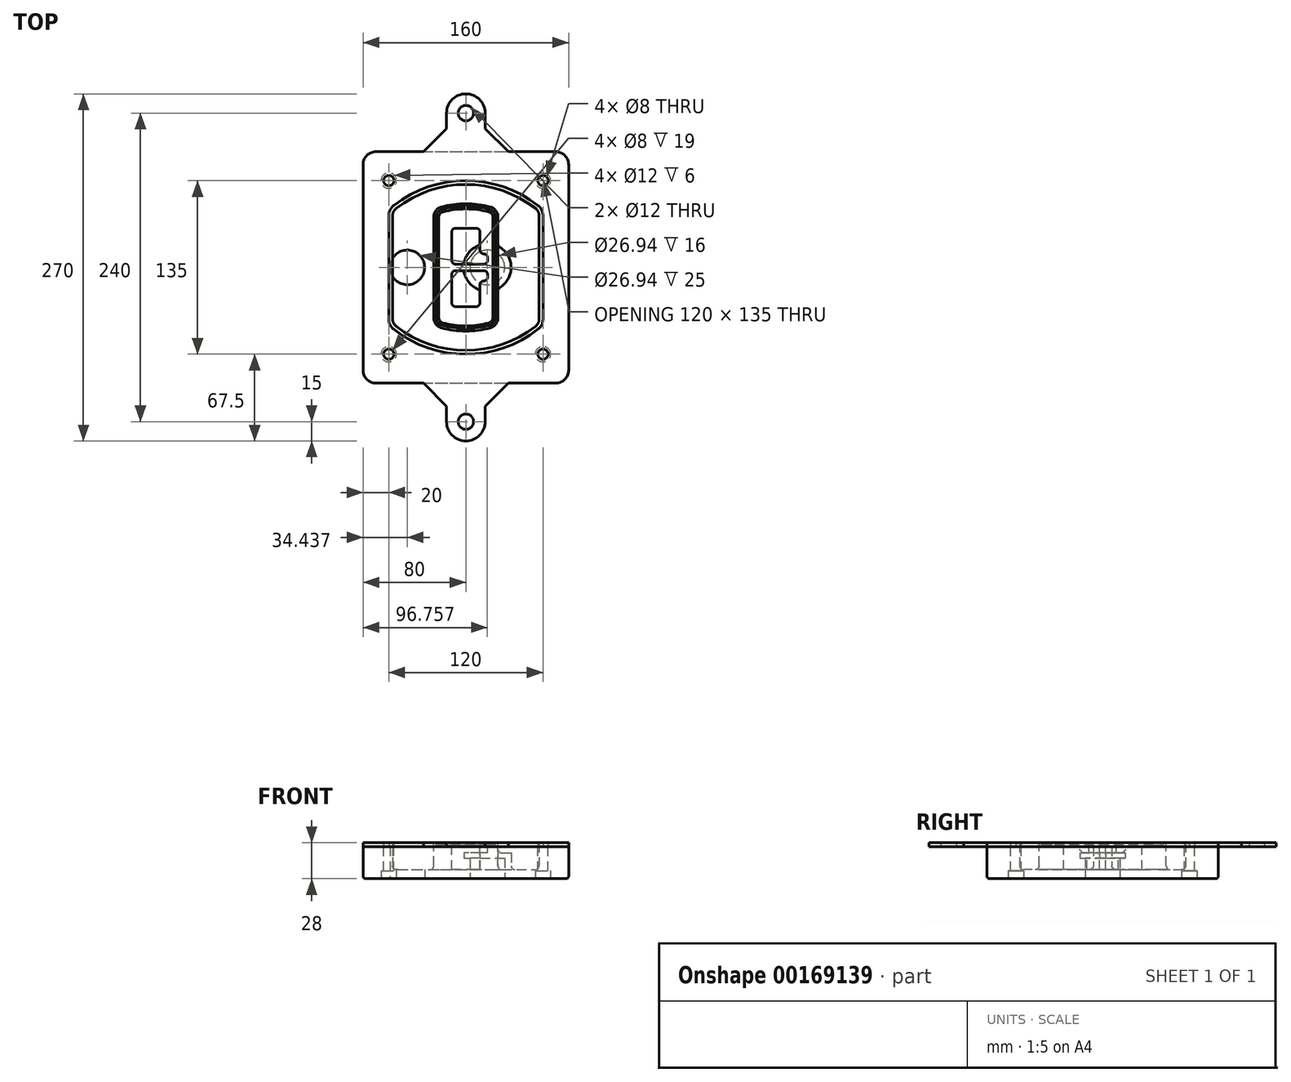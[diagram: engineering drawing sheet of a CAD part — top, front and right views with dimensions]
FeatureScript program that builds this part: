
annotation { "Feature Type Name" : "Feature", "Feature Type Description" : "" }
export const myFeature = defineFeature(function(context is Context, id is Id, definition is map)
    precondition{}
    {
        {
            var Q0;
            Q0=qCreatedBy(makeId("Top.planeOp"),FACE);
            var sketch = newSketch(context, id + "F0", { "sketchPlane" : qUnion([Q0])});
            skPoint(sketch, "E0.rect.middle", {"position": v(0, 0) * mm});
            skLineSegment(sketch, "E1.bottom", {"start": v(-70, -90) * mm, "end": v(70, -90) * mm});
            skLineSegment(sketch, "E1.top", {"start": v(-70, 90) * mm, "end": v(70, 90) * mm});
            skLineSegment(sketch, "E1.left", {"start": v(-80, -80) * mm, "end": v(-80, 80) * mm});
            skLineSegment(sketch, "E1.right", {"start": v(80, -80) * mm, "end": v(80, 80) * mm});
            skLineSegment(sketch, "E2", {"start": v(-80, 90) * mm, "end": v(80, -90) * mm, "construction": true});
            skLineSegment(sketch, "E3", {"start": v(80, 90) * mm, "end": v(-80, -90) * mm, "construction": true});
            skCircle(sketch, "E4", {"center": v(-60, 67.5) * mm, "radius": 4 * mm});
            skCircle(sketch, "E5", {"center": v(60, 67.5) * mm, "radius": 4 * mm});
            skCircle(sketch, "E6", {"center": v(60, -67.5) * mm, "radius": 4 * mm});
            skCircle(sketch, "E7", {"center": v(-60, -67.5) * mm, "radius": 4 * mm});
            skLineSegment(sketch, "E8", {"start": v(-60, 67.5) * mm, "end": v(60, 67.5) * mm, "construction": true});
            skLineSegment(sketch, "E9", {"start": v(60, 67.5) * mm, "end": v(60, -67.5) * mm, "construction": true});
            skLineSegment(sketch, "E10", {"start": v(60, -67.5) * mm, "end": v(-60, -67.5) * mm, "construction": true});
            skLineSegment(sketch, "E11", {"start": v(-60, -67.5) * mm, "end": v(-60, 67.5) * mm, "construction": true});
            skLineSegment(sketch, "E12", {"start": v(-60, 40.3) * mm, "end": v(-60, -40.3) * mm});
            skLineSegment(sketch, "E13", {"start": v(60, 40.3) * mm, "end": v(60, -40.3) * mm});
            skArc(sketch, "E14", {"start": v(56.15, 48.18) * mm, "mid": v(0, 67.5) * mm, "end": v(-56.15, 48.18) * mm});
            skArc(sketch, "E15", {"start": v(-56.15, -48.18) * mm, "mid": v(0, -67.5) * mm, "end": v(56.15, -48.18) * mm});
            skLineSegment(sketch, "E16", {"start": v(-60, 0) * mm, "end": v(60, 0) * mm, "construction": true});
            skPoint(sketch, "E17.visualSharp", {"position": v(-60, -45) * mm});
            skArc(sketch, "E17.filletArc", {"start": v(-60, -40.3) * mm, "mid": v(-58.99, -44.68) * mm, "end": v(-56.15, -48.18) * mm});
            skPoint(sketch, "E18.visualSharp", {"position": v(-60, 45) * mm});
            skArc(sketch, "E18.filletArc", {"start": v(-56.15, 48.18) * mm, "mid": v(-58.99, 44.68) * mm, "end": v(-60, 40.3) * mm});
            skPoint(sketch, "E19.visualSharp", {"position": v(60, 45) * mm});
            skArc(sketch, "E19.filletArc", {"start": v(60, 40.3) * mm, "mid": v(58.99, 44.68) * mm, "end": v(56.15, 48.18) * mm});
            skPoint(sketch, "E20.visualSharp", {"position": v(60, -45) * mm});
            skArc(sketch, "E20.filletArc", {"start": v(56.15, -48.18) * mm, "mid": v(58.99, -44.68) * mm, "end": v(60, -40.3) * mm});
            skPoint(sketch, "E21.visualSharp", {"position": v(-80, 90) * mm});
            skArc(sketch, "E21.filletArc", {"start": v(-70, 90) * mm, "mid": v(-77.07, 87.07) * mm, "end": v(-80, 80) * mm});
            skPoint(sketch, "E22.visualSharp", {"position": v(80, 90) * mm});
            skArc(sketch, "E22.filletArc", {"start": v(80, 80) * mm, "mid": v(77.07, 87.07) * mm, "end": v(70, 90) * mm});
            skPoint(sketch, "E23.visualSharp", {"position": v(80, -90) * mm});
            skArc(sketch, "E23.filletArc", {"start": v(70, -90) * mm, "mid": v(77.07, -87.07) * mm, "end": v(80, -80) * mm});
            skPoint(sketch, "E24.visualSharp", {"position": v(-80, -90) * mm});
            skArc(sketch, "E24.filletArc", {"start": v(-80, -80) * mm, "mid": v(-77.07, -87.07) * mm, "end": v(-70, -90) * mm});
            skArc(sketch, "E25.0", {"start": v(57, 40.3) * mm, "mid": v(56.3, 43.36) * mm, "end": v(54.3, 45.81) * mm});
            skLineSegment(sketch, "E25.1", {"start": v(57, 40.3) * mm, "end": v(57, -40.3) * mm});
            skArc(sketch, "E25.2", {"start": v(54.3, -45.81) * mm, "mid": v(56.3, -43.36) * mm, "end": v(57, -40.3) * mm});
            skArc(sketch, "E25.3", {"start": v(-54.3, -45.81) * mm, "mid": v(0, -64.5) * mm, "end": v(54.3, -45.81) * mm});
            skArc(sketch, "E25.4", {"start": v(-57, -40.3) * mm, "mid": v(-56.3, -43.36) * mm, "end": v(-54.3, -45.81) * mm});
            skArc(sketch, "E25.5", {"start": v(54.3, 45.81) * mm, "mid": v(0, 64.5) * mm, "end": v(-54.3, 45.81) * mm});
            skLineSegment(sketch, "E25.6", {"start": v(-57, 40.3) * mm, "end": v(-57, -40.3) * mm});
            skArc(sketch, "E25.7", {"start": v(-54.3, 45.81) * mm, "mid": v(-56.3, 43.36) * mm, "end": v(-57, 40.3) * mm});
            skArc(sketch, "E26.0", {"start": v(-58.62, 51.33) * mm, "mid": v(-62.58, 46.43) * mm, "end": v(-64, 40.3) * mm});
            skArc(sketch, "E26.1", {"start": v(58.62, 51.33) * mm, "mid": v(0, 71.5) * mm, "end": v(-58.62, 51.33) * mm});
            skArc(sketch, "E26.2", {"start": v(64, 40.3) * mm, "mid": v(62.58, 46.43) * mm, "end": v(58.62, 51.33) * mm});
            skLineSegment(sketch, "E26.3", {"start": v(64, 40.3) * mm, "end": v(64, -40.3) * mm});
            skArc(sketch, "E26.4", {"start": v(58.62, -51.33) * mm, "mid": v(62.58, -46.43) * mm, "end": v(64, -40.3) * mm});
            skLineSegment(sketch, "E26.5", {"start": v(-64, 40.3) * mm, "end": v(-64, -40.3) * mm});
            skArc(sketch, "E26.6", {"start": v(-58.62, -51.33) * mm, "mid": v(0, -71.5) * mm, "end": v(58.62, -51.33) * mm});
            skArc(sketch, "E26.7", {"start": v(-64, -40.3) * mm, "mid": v(-62.58, -46.43) * mm, "end": v(-58.62, -51.33) * mm});
            skSolve(sketch);
        }
        {
            var Q0;
            Q0=makeQuery(id+"F0.imprint","IMPRINT",FACE,{"disambiguationData":[TD([[makeQuery(id+"F0.imprint","IMPRINT",EDGE,{"derivedFrom":sQuery(id+"F0.wireOp",EDGE,"E1.bottom")}),1.0]])]});
            var Q1;
            Q1=makeQuery(id+"F0.imprint","IMPRINT",FACE,{"disambiguationData":[TD([[makeQuery(id+"F0.imprint","IMPRINT",EDGE,{"derivedFrom":sQuery(id+"F0.wireOp",EDGE,"E12")}),1.0]])]});
            var Q2;
            Q2=makeQuery(id+"F0.imprint","IMPRINT",FACE,{"disambiguationData":[TD([[makeQuery(id+"F0.imprint","IMPRINT",EDGE,{"derivedFrom":sQuery(id+"F0.wireOp",EDGE,"E25.0")}),1.0]])]});
            var Q3;
            Q3=makeQuery(id+"F0.imprint","IMPRINT",FACE,{"disambiguationData":[TD([[makeQuery(id+"F0.imprint","IMPRINT",EDGE,{"derivedFrom":sQuery(id+"F0.wireOp",EDGE,"E12")}),-1.0]])]});
            extrude(context, id + "F1", {"entities" : qUnion([Q0, Q1, Q2, Q3]), "oppositeDirection" : true, "depth" : 25 * mm});
        }
        {
            var Q0;
            Q0=makeQuery(id+"F0.imprint","IMPRINT",FACE,{"disambiguationData":[TD([[makeQuery(id+"F0.imprint","IMPRINT",EDGE,{"derivedFrom":sQuery(id+"F0.wireOp",EDGE,"E12")}),1.0]])]});
            extrude(context, id + "F2", {"entities" : qUnion([Q0]), "operationType" : NewBodyOperationType.ADD, "depth" : 3 * mm});
        }
        {
            var Q0;
            Q0=makeQuery(id+"F0.imprint","IMPRINT",FACE,{"disambiguationData":[TD([[makeQuery(id+"F0.imprint","IMPRINT",EDGE,{"derivedFrom":sQuery(id+"F0.wireOp",EDGE,"E25.0")}),1.0]])]});
            extrude(context, id + "F3", {"entities" : qUnion([Q0]), "operationType" : NewBodyOperationType.REMOVE, "oppositeDirection" : true, "depth" : 18 * mm});
        }
        {
            var Q0;
            Q0=makeQuery(id+"F2.opExtrude","CAP_FACE",FACE,{"disambiguationData":[OSD([sQuery(id+"F0.wireOp",EDGE,"E12"),sQuery(id+"F0.wireOp",EDGE,"E13"),sQuery(id+"F0.wireOp",EDGE,"E14"),sQuery(id+"F0.wireOp",EDGE,"E15"),sQuery(id+"F0.wireOp",EDGE,"E17.filletArc"),sQuery(id+"F0.wireOp",EDGE,"E18.filletArc"),sQuery(id+"F0.wireOp",EDGE,"E19.filletArc"),sQuery(id+"F0.wireOp",EDGE,"E20.filletArc"),sQuery(id+"F0.wireOp",EDGE,"E25.0"),sQuery(id+"F0.wireOp",EDGE,"E25.1"),sQuery(id+"F0.wireOp",EDGE,"E25.2"),sQuery(id+"F0.wireOp",EDGE,"E25.3"),sQuery(id+"F0.wireOp",EDGE,"E25.4"),sQuery(id+"F0.wireOp",EDGE,"E25.5"),sQuery(id+"F0.wireOp",EDGE,"E25.6"),sQuery(id+"F0.wireOp",EDGE,"E25.7")])],"isStart":false});
            var sketch = newSketch(context, id + "F4", { "sketchPlane" : qUnion([Q0])});
            skArc(sketch, "E27.0", {"start": v(-19.08, -46.97) * mm, "mid": v(0, -49.5) * mm, "end": v(19.08, -46.97) * mm});
            skArc(sketch, "E28.0", {"start": v(19.08, 46.97) * mm, "mid": v(0, 49.5) * mm, "end": v(-19.08, 46.97) * mm});
            skLineSegment(sketch, "E29", {"start": v(-25, 39.25) * mm, "end": v(-25, -39.25) * mm});
            skLineSegment(sketch, "E30", {"start": v(25, 39.25) * mm, "end": v(25, -39.25) * mm});
            skLineSegment(sketch, "E31", {"start": v(-25, 45.1) * mm, "end": v(25, 45.1) * mm, "construction": true});
            skLineSegment(sketch, "E32", {"start": v(-25, -45.1) * mm, "end": v(25, -45.1) * mm, "construction": true});
            skPoint(sketch, "E33.visualSharp", {"position": v(-25, 45.1) * mm});
            skArc(sketch, "E33.filletArc", {"start": v(-19.08, 46.97) * mm, "mid": v(-23.35, 44.11) * mm, "end": v(-25, 39.25) * mm});
            skPoint(sketch, "E34.visualSharp", {"position": v(25, 45.1) * mm});
            skArc(sketch, "E34.filletArc", {"start": v(25, 39.25) * mm, "mid": v(23.35, 44.11) * mm, "end": v(19.08, 46.97) * mm});
            skPoint(sketch, "E35.visualSharp", {"position": v(25, -45.1) * mm});
            skArc(sketch, "E35.filletArc", {"start": v(19.08, -46.97) * mm, "mid": v(23.35, -44.11) * mm, "end": v(25, -39.25) * mm});
            skPoint(sketch, "E36.visualSharp", {"position": v(-25, -45.1) * mm});
            skArc(sketch, "E36.filletArc", {"start": v(-25, -39.25) * mm, "mid": v(-23.35, -44.11) * mm, "end": v(-19.08, -46.97) * mm});
            skArc(sketch, "E37.0", {"start": v(54.3, 45.81) * mm, "mid": v(0, 64.5) * mm, "end": v(-54.3, 45.81) * mm});
            skArc(sketch, "E37.1", {"start": v(-54.3, 45.81) * mm, "mid": v(-56.3, 43.36) * mm, "end": v(-57, 40.3) * mm});
            skLineSegment(sketch, "E37.2", {"start": v(-57, 40.3) * mm, "end": v(-57, -40.3) * mm});
            skArc(sketch, "E37.3", {"start": v(-57, -40.3) * mm, "mid": v(-56.3, -43.36) * mm, "end": v(-54.3, -45.81) * mm});
            skArc(sketch, "E37.4", {"start": v(-54.3, -45.81) * mm, "mid": v(0, -64.5) * mm, "end": v(54.3, -45.81) * mm});
            skArc(sketch, "E37.5", {"start": v(54.3, -45.81) * mm, "mid": v(56.3, -43.36) * mm, "end": v(57, -40.3) * mm});
            skLineSegment(sketch, "E37.6", {"start": v(57, 40.3) * mm, "end": v(57, -40.3) * mm});
            skArc(sketch, "E37.7", {"start": v(57, 40.3) * mm, "mid": v(56.3, 43.36) * mm, "end": v(54.3, 45.81) * mm});
            skLineSegment(sketch, "E38.0", {"start": v(23, 39.25) * mm, "end": v(23, -39.25) * mm});
            skArc(sketch, "E38.1", {"start": v(18.56, -45.04) * mm, "mid": v(21.76, -42.9) * mm, "end": v(23, -39.25) * mm});
            skArc(sketch, "E38.2", {"start": v(-18.56, -45.04) * mm, "mid": v(0, -47.5) * mm, "end": v(18.56, -45.04) * mm});
            skArc(sketch, "E38.3", {"start": v(-23, -39.25) * mm, "mid": v(-21.76, -42.9) * mm, "end": v(-18.56, -45.04) * mm});
            skLineSegment(sketch, "E38.4", {"start": v(-23, 39.25) * mm, "end": v(-23, -39.25) * mm});
            skArc(sketch, "E38.5", {"start": v(23, 39.25) * mm, "mid": v(21.76, 42.9) * mm, "end": v(18.56, 45.04) * mm});
            skArc(sketch, "E38.6", {"start": v(-18.56, 45.04) * mm, "mid": v(-21.76, 42.9) * mm, "end": v(-23, 39.25) * mm});
            skArc(sketch, "E38.7", {"start": v(18.56, 45.04) * mm, "mid": v(0, 47.5) * mm, "end": v(-18.56, 45.04) * mm});
            skArc(sketch, "E39.0", {"start": v(21, 39.25) * mm, "mid": v(20.18, 41.68) * mm, "end": v(18.04, 43.1) * mm});
            skLineSegment(sketch, "E39.1", {"start": v(21, 39.25) * mm, "end": v(21, -39.25) * mm});
            skArc(sketch, "E39.2", {"start": v(18.04, -43.1) * mm, "mid": v(20.18, -41.68) * mm, "end": v(21, -39.25) * mm});
            skArc(sketch, "E39.3", {"start": v(-18.04, -43.1) * mm, "mid": v(0, -45.5) * mm, "end": v(18.04, -43.1) * mm});
            skArc(sketch, "E39.4", {"start": v(-21, -39.25) * mm, "mid": v(-20.18, -41.68) * mm, "end": v(-18.04, -43.1) * mm});
            skArc(sketch, "E39.5", {"start": v(18.04, 43.1) * mm, "mid": v(0, 45.5) * mm, "end": v(-18.04, 43.1) * mm});
            skLineSegment(sketch, "E39.6", {"start": v(-21, 39.25) * mm, "end": v(-21, -39.25) * mm});
            skArc(sketch, "E39.7", {"start": v(-18.04, 43.1) * mm, "mid": v(-20.18, 41.68) * mm, "end": v(-21, 39.25) * mm});
            skLineSegment(sketch, "E40", {"start": v(-25, 0) * mm, "end": v(25, 0) * mm, "construction": true});
            skLineSegment(sketch, "E41", {"start": v(-11, 5.5) * mm, "end": v(-11, 27.5) * mm});
            skLineSegment(sketch, "E42", {"start": v(-8, 30.5) * mm, "end": v(8, 30.5) * mm});
            skLineSegment(sketch, "E43", {"start": v(11, 27.5) * mm, "end": v(11, 13.5) * mm});
            skLineSegment(sketch, "E44", {"start": v(14, 10.5) * mm, "end": v(14, 10.5) * mm});
            skLineSegment(sketch, "E45", {"start": v(17, 7.5) * mm, "end": v(17, 5.5) * mm});
            skLineSegment(sketch, "E46", {"start": v(14, 2.5) * mm, "end": v(-8, 2.5) * mm});
            skPoint(sketch, "E47.visualSharp", {"position": v(-11, 30.5) * mm});
            skArc(sketch, "E47.filletArc", {"start": v(-8, 30.5) * mm, "mid": v(-10.12, 29.62) * mm, "end": v(-11, 27.5) * mm});
            skPoint(sketch, "E48.visualSharp", {"position": v(11, 30.5) * mm});
            skArc(sketch, "E48.filletArc", {"start": v(11, 27.5) * mm, "mid": v(10.12, 29.62) * mm, "end": v(8, 30.5) * mm});
            skPoint(sketch, "E49.visualSharp", {"position": v(11, 10.5) * mm});
            skArc(sketch, "E49.filletArc", {"start": v(11, 13.5) * mm, "mid": v(11.88, 11.38) * mm, "end": v(14, 10.5) * mm});
            skPoint(sketch, "E50.visualSharp", {"position": v(17, 10.5) * mm});
            skArc(sketch, "E50.filletArc", {"start": v(17, 7.5) * mm, "mid": v(16.12, 9.62) * mm, "end": v(14, 10.5) * mm});
            skPoint(sketch, "E51.visualSharp", {"position": v(17, 2.5) * mm});
            skArc(sketch, "E51.filletArc", {"start": v(14, 2.5) * mm, "mid": v(16.12, 3.38) * mm, "end": v(17, 5.5) * mm});
            skPoint(sketch, "E52.visualSharp", {"position": v(-11, 2.5) * mm});
            skArc(sketch, "E52.filletArc", {"start": v(-11, 5.5) * mm, "mid": v(-10.12, 3.38) * mm, "end": v(-8, 2.5) * mm});
            skLineSegment(sketch, "E53.0.MirrorCS", {"start": v(14, -2.5) * mm, "end": v(-8, -2.5) * mm});
            skArc(sketch, "E54.0.MirrorCS", {"start": v(-11, -5.5) * mm, "mid": v(-10.12, -3.38) * mm, "end": v(-8, -2.5) * mm});
            skLineSegment(sketch, "E55.0.MirrorCS", {"start": v(-11, -5.5) * mm, "end": v(-11, -27.5) * mm});
            skArc(sketch, "E56.0.MirrorCS", {"start": v(-8, -30.5) * mm, "mid": v(-10.12, -29.62) * mm, "end": v(-11, -27.5) * mm});
            skLineSegment(sketch, "E57.0.MirrorCS", {"start": v(-8, -30.5) * mm, "end": v(8, -30.5) * mm});
            skArc(sketch, "E58.0.MirrorCS", {"start": v(11, -27.5) * mm, "mid": v(10.12, -29.62) * mm, "end": v(8, -30.5) * mm});
            skLineSegment(sketch, "E59.0.MirrorCS", {"start": v(11, -27.5) * mm, "end": v(11, -13.5) * mm});
            skArc(sketch, "E60.0.MirrorCS", {"start": v(11, -13.5) * mm, "mid": v(11.88, -11.38) * mm, "end": v(14, -10.5) * mm});
            skArc(sketch, "E61.0.MirrorCS", {"start": v(17, -7.5) * mm, "mid": v(16.12, -9.62) * mm, "end": v(14, -10.5) * mm});
            skLineSegment(sketch, "E62.0.MirrorCS", {"start": v(17, -7.5) * mm, "end": v(17, -5.5) * mm});
            skArc(sketch, "E63.0.MirrorCS", {"start": v(14, -2.5) * mm, "mid": v(16.12, -3.38) * mm, "end": v(17, -5.5) * mm});
            skSolve(sketch);
        }
        {
            var Q0;
            Q0=makeQuery(id+"F4.imprint","IMPRINT",FACE,{"disambiguationData":[TD([[makeQuery(id+"F4.imprint","IMPRINT",EDGE,{"derivedFrom":sQuery(id+"F4.wireOp",EDGE,"E27.0")}),1.0]])]});
            var Q1;
            Q1=makeQuery(id+"F4.imprint","IMPRINT",FACE,{"disambiguationData":[TD([[makeQuery(id+"F4.imprint","IMPRINT",EDGE,{"derivedFrom":sQuery(id+"F4.wireOp",EDGE,"E38.0")}),-1.0]])]});
            var Q2;
            Q2=makeQuery(id+"F4.imprint","IMPRINT",FACE,{"disambiguationData":[TD([[makeQuery(id+"F4.imprint","IMPRINT",EDGE,{"derivedFrom":sQuery(id+"F4.wireOp",EDGE,"E39.0")}),1.0]])]});
            extrude(context, id + "F5", {"entities" : qUnion([Q0, Q1, Q2]), "operationType" : NewBodyOperationType.ADD, "endBound" : BoundingType.UP_TO_NEXT, "oppositeDirection" : true, "depth" : 25 * mm});
        }
        {
            var Q0;
            Q0=makeQuery(id+"F4.imprint","IMPRINT",FACE,{"disambiguationData":[TD([[makeQuery(id+"F4.imprint","IMPRINT",EDGE,{"derivedFrom":sQuery(id+"F4.wireOp",EDGE,"E38.0")}),-1.0]])]});
            extrude(context, id + "F6", {"entities" : qUnion([Q0]), "operationType" : NewBodyOperationType.REMOVE, "oppositeDirection" : true, "depth" : 2 * mm});
        }
        {
            var Q0;
            Q0=makeQuery(id+"F1.opExtrude","CAP_FACE",FACE,{"disambiguationData":[OSD([sQuery(id+"F0.wireOp",EDGE,"E1.bottom"),sQuery(id+"F0.wireOp",EDGE,"E1.top"),sQuery(id+"F0.wireOp",EDGE,"E1.left"),sQuery(id+"F0.wireOp",EDGE,"E1.right"),sQuery(id+"F0.wireOp",EDGE,"E4"),sQuery(id+"F0.wireOp",EDGE,"E5"),sQuery(id+"F0.wireOp",EDGE,"E6"),sQuery(id+"F0.wireOp",EDGE,"E7"),sQuery(id+"F0.wireOp",EDGE,"E21.filletArc"),sQuery(id+"F0.wireOp",EDGE,"E22.filletArc"),sQuery(id+"F0.wireOp",EDGE,"E23.filletArc"),sQuery(id+"F0.wireOp",EDGE,"E24.filletArc")])],"isStart":false});
            var sketch = newSketch(context, id + "F7", { "sketchPlane" : qUnion([Q0])});
            skCircle(sketch, "E64", {"center": v(16.76, 0) * mm, "radius": 13.47 * mm});
            skCircle(sketch, "E65", {"center": v(-45.56, 0) * mm, "radius": 13.47 * mm});
            skLineSegment(sketch, "E66", {"start": v(80, 0) * mm, "end": v(-80, 0) * mm});
            skCircle(sketch, "E67", {"center": v(16.76, 0) * mm, "radius": 18.47 * mm});
            skCircle(sketch, "E68", {"center": v(60, -67.5) * mm, "radius": 6 * mm});
            skCircle(sketch, "E69", {"center": v(-60, -67.5) * mm, "radius": 6 * mm});
            skCircle(sketch, "E70", {"center": v(-60, 67.5) * mm, "radius": 6 * mm});
            skCircle(sketch, "E71", {"center": v(60, 67.5) * mm, "radius": 6 * mm});
            skSolve(sketch);
        }
        {
            var Q0;
            {var subQ1=sQuery(id+"F7.wireOp",EDGE,"E66");var subQ4=sQuery(id+"F7.wireOp",EDGE,"E64");var subQ6=makeQuery(id+"F7.imprint","INTERSECT",VERTEX,{"disambiguationData":[OD(0.0)],"derivedFrom":[subQ4,subQ1]});Q0=makeQuery(id+"F7.imprint","IMPRINT",FACE,{"disambiguationData":[TD([[makeQuery(id+"F7.imprint","IMPRINT",EDGE,{"disambiguationData":[TD([[subQ6,-1.0]])],"derivedFrom":subQ4}),-1.0]])]});}
            var Q1;
            {var subQ0=sQuery(id+"F7.wireOp",EDGE,"E66");var subQ1=sQuery(id+"F7.wireOp",EDGE,"E64");var subQ3=makeQuery(id+"F7.imprint","INTERSECT",VERTEX,{"disambiguationData":[OD(0.0)],"derivedFrom":[subQ1,subQ0]});Q1=makeQuery(id+"F7.imprint","IMPRINT",FACE,{"disambiguationData":[TD([[makeQuery(id+"F7.imprint","IMPRINT",EDGE,{"disambiguationData":[TD([[subQ3,-1.0]])],"derivedFrom":subQ1}),1.0]])]});}
            var Q2;
            {var subQ0=sQuery(id+"F7.wireOp",EDGE,"E66");var subQ1=sQuery(id+"F7.wireOp",EDGE,"E64");var subQ3=makeQuery(id+"F7.imprint","INTERSECT",VERTEX,{"disambiguationData":[OD(0.0)],"derivedFrom":[subQ1,subQ0]});Q2=makeQuery(id+"F7.imprint","IMPRINT",FACE,{"disambiguationData":[TD([[makeQuery(id+"F7.imprint","IMPRINT",EDGE,{"disambiguationData":[TD([[subQ3,1.0]])],"derivedFrom":subQ1}),1.0]])]});}
            var Q3;
            {var subQ1=sQuery(id+"F7.wireOp",EDGE,"E66");var subQ4=sQuery(id+"F7.wireOp",EDGE,"E64");var subQ6=makeQuery(id+"F7.imprint","INTERSECT",VERTEX,{"disambiguationData":[OD(0.0)],"derivedFrom":[subQ4,subQ1]});Q3=makeQuery(id+"F7.imprint","IMPRINT",FACE,{"disambiguationData":[TD([[makeQuery(id+"F7.imprint","IMPRINT",EDGE,{"disambiguationData":[TD([[subQ6,1.0]])],"derivedFrom":subQ4}),-1.0]])]});}
            extrude(context, id + "F8", {"entities" : qUnion([Q0, Q1, Q2, Q3]), "operationType" : NewBodyOperationType.ADD, "oppositeDirection" : true, "depth" : 20 * mm});
        }
        {
            var Q0;
            {var subQ0=sQuery(id+"F7.wireOp",EDGE,"E66");var subQ1=sQuery(id+"F7.wireOp",EDGE,"E64");var subQ3=makeQuery(id+"F7.imprint","INTERSECT",VERTEX,{"disambiguationData":[OD(0.0)],"derivedFrom":[subQ1,subQ0]});Q0=makeQuery(id+"F7.imprint","IMPRINT",FACE,{"disambiguationData":[TD([[makeQuery(id+"F7.imprint","IMPRINT",EDGE,{"disambiguationData":[TD([[subQ3,-1.0]])],"derivedFrom":subQ1}),1.0]])]});}
            var Q1;
            {var subQ0=sQuery(id+"F7.wireOp",EDGE,"E66");var subQ1=sQuery(id+"F7.wireOp",EDGE,"E64");var subQ3=makeQuery(id+"F7.imprint","INTERSECT",VERTEX,{"disambiguationData":[OD(0.0)],"derivedFrom":[subQ1,subQ0]});Q1=makeQuery(id+"F7.imprint","IMPRINT",FACE,{"disambiguationData":[TD([[makeQuery(id+"F7.imprint","IMPRINT",EDGE,{"disambiguationData":[TD([[subQ3,1.0]])],"derivedFrom":subQ1}),1.0]])]});}
            extrude(context, id + "F9", {"entities" : qUnion([Q0, Q1]), "operationType" : NewBodyOperationType.REMOVE, "oppositeDirection" : true, "depth" : 16 * mm});
        }
        {
            var Q0;
            {var subQ0=sQuery(id+"F7.wireOp",EDGE,"E66");var subQ1=sQuery(id+"F7.wireOp",EDGE,"E65");var subQ3=makeQuery(id+"F7.imprint","INTERSECT",VERTEX,{"disambiguationData":[OD(0.0)],"derivedFrom":[subQ1,subQ0]});Q0=makeQuery(id+"F7.imprint","IMPRINT",FACE,{"disambiguationData":[TD([[makeQuery(id+"F7.imprint","IMPRINT",EDGE,{"disambiguationData":[TD([[subQ3,-1.0]])],"derivedFrom":subQ1}),1.0]])]});}
            var Q1;
            {var subQ0=sQuery(id+"F7.wireOp",EDGE,"E66");var subQ1=sQuery(id+"F7.wireOp",EDGE,"E65");var subQ3=makeQuery(id+"F7.imprint","INTERSECT",VERTEX,{"disambiguationData":[OD(0.0)],"derivedFrom":[subQ1,subQ0]});Q1=makeQuery(id+"F7.imprint","IMPRINT",FACE,{"disambiguationData":[TD([[makeQuery(id+"F7.imprint","IMPRINT",EDGE,{"disambiguationData":[TD([[subQ3,1.0]])],"derivedFrom":subQ1}),1.0]])]});}
            extrude(context, id + "F10", {"entities" : qUnion([Q0, Q1]), "operationType" : NewBodyOperationType.REMOVE, "oppositeDirection" : true, "depth" : 25 * mm});
        }
        {
            var Q0;
            Q0=makeQuery(id+"F7.imprint","IMPRINT",FACE,{"disambiguationData":[TD([[makeQuery(id+"F7.imprint","IMPRINT",EDGE,{"derivedFrom":sQuery(id+"F7.wireOp",EDGE,"E68")}),1.0]])]});
            var Q1;
            Q1=makeQuery(id+"F7.imprint","IMPRINT",FACE,{"disambiguationData":[TD([[makeQuery(id+"F7.imprint","IMPRINT",EDGE,{"derivedFrom":makeQuery(id+"F1.opExtrude","CAP_EDGE",EDGE,{"disambiguationData":[OSD([sQuery(id+"F0.wireOp",EDGE,"E5")])],"isStart":false})}),-1.0]])]});
            var Q2;
            Q2=makeQuery(id+"F7.imprint","IMPRINT",FACE,{"disambiguationData":[TD([[makeQuery(id+"F7.imprint","IMPRINT",EDGE,{"derivedFrom":sQuery(id+"F7.wireOp",EDGE,"E69")}),1.0]])]});
            var Q3;
            Q3=makeQuery(id+"F7.imprint","IMPRINT",FACE,{"disambiguationData":[TD([[makeQuery(id+"F7.imprint","IMPRINT",EDGE,{"derivedFrom":makeQuery(id+"F1.opExtrude","CAP_EDGE",EDGE,{"disambiguationData":[OSD([sQuery(id+"F0.wireOp",EDGE,"E4")])],"isStart":false})}),-1.0]])]});
            var Q4;
            Q4=makeQuery(id+"F7.imprint","IMPRINT",FACE,{"disambiguationData":[TD([[makeQuery(id+"F7.imprint","IMPRINT",EDGE,{"derivedFrom":sQuery(id+"F7.wireOp",EDGE,"E70")}),1.0]])]});
            var Q5;
            Q5=makeQuery(id+"F7.imprint","IMPRINT",FACE,{"disambiguationData":[TD([[makeQuery(id+"F7.imprint","IMPRINT",EDGE,{"derivedFrom":makeQuery(id+"F1.opExtrude","CAP_EDGE",EDGE,{"disambiguationData":[OSD([sQuery(id+"F0.wireOp",EDGE,"E7")])],"isStart":false})}),-1.0]])]});
            var Q6;
            Q6=makeQuery(id+"F7.imprint","IMPRINT",FACE,{"disambiguationData":[TD([[makeQuery(id+"F7.imprint","IMPRINT",EDGE,{"derivedFrom":sQuery(id+"F7.wireOp",EDGE,"E71")}),1.0]])]});
            var Q7;
            Q7=makeQuery(id+"F7.imprint","IMPRINT",FACE,{"disambiguationData":[TD([[makeQuery(id+"F7.imprint","IMPRINT",EDGE,{"derivedFrom":makeQuery(id+"F1.opExtrude","CAP_EDGE",EDGE,{"disambiguationData":[OSD([sQuery(id+"F0.wireOp",EDGE,"E6")])],"isStart":false})}),-1.0]])]});
            extrude(context, id + "F11", {"entities" : qUnion([Q0, Q1, Q2, Q3, Q4, Q5, Q6, Q7]), "operationType" : NewBodyOperationType.REMOVE, "oppositeDirection" : true, "depth" : 6 * mm});
        }
        {
            var Q0;
            Q0=makeQuery(id+"F9.boolean.opBoolean","COPY",FACE,{"derivedFrom":makeQuery(id+"F9.opExtrude","CAP_FACE",FACE,{"disambiguationData":[OSD([sQuery(id+"F7.wireOp",EDGE,"E64")])],"isStart":false})});
            var sketch = newSketch(context, id + "F12", { "sketchPlane" : qUnion([Q0])});
            skArc(sketch, "E72.0", {"start": v(11, 17.55) * mm, "mid": v(2.57, 11.82) * mm, "end": v(-1.54, 2.5) * mm});
            skArc(sketch, "E72.1", {"start": v(-1.54, -2.5) * mm, "mid": v(2.57, -11.82) * mm, "end": v(11, -17.55) * mm});
            skLineSegment(sketch, "E73", {"start": v(-1.54, -2.5) * mm, "end": v(14, -2.5) * mm});
            skLineSegment(sketch, "E74.0", {"start": v(14, 2.5) * mm, "end": v(-1.54, 2.5) * mm});
            skArc(sketch, "E74.1", {"start": v(14, 2.5) * mm, "mid": v(16.12, 3.38) * mm, "end": v(17, 5.5) * mm});
            skLineSegment(sketch, "E74.2", {"start": v(17, 7.5) * mm, "end": v(17, 5.5) * mm});
            skArc(sketch, "E74.3", {"start": v(17, 7.5) * mm, "mid": v(16.12, 9.62) * mm, "end": v(14, 10.5) * mm});
            skArc(sketch, "E74.4", {"start": v(11, 13.5) * mm, "mid": v(11.88, 11.38) * mm, "end": v(14, 10.5) * mm});
            skLineSegment(sketch, "E74.5", {"start": v(11, 17.55) * mm, "end": v(11, 13.5) * mm});
            skLineSegment(sketch, "E74.7", {"start": v(14, -2.5) * mm, "end": v(-1.54, -2.5) * mm});
            skArc(sketch, "E74.8", {"start": v(14, -2.5) * mm, "mid": v(16.12, -3.38) * mm, "end": v(17, -5.5) * mm});
            skLineSegment(sketch, "E74.9", {"start": v(17, -7.5) * mm, "end": v(17, -5.5) * mm});
            skArc(sketch, "E74.10", {"start": v(17, -7.5) * mm, "mid": v(16.12, -9.62) * mm, "end": v(14, -10.5) * mm});
            skArc(sketch, "E74.11", {"start": v(11, -13.5) * mm, "mid": v(11.88, -11.38) * mm, "end": v(14, -10.5) * mm});
            skLineSegment(sketch, "E74.12", {"start": v(11, -17.55) * mm, "end": v(11, -13.5) * mm});
            skPoint(sketch, "E75.orphan", {"position": v(11, -27.5) * mm});
            skPoint(sketch, "E76.orphan", {"position": v(-8, -2.5) * mm});
            skPoint(sketch, "E77.orphan", {"position": v(-8, 2.5) * mm});
            skPoint(sketch, "E78.orphan", {"position": v(11, 27.5) * mm});
            skSolve(sketch);
        }
        {
            var Q0;
            {var subQ7=sQuery(id+"F12.wireOp",EDGE,"E72.0");var subQ14=sQuery(id+"F12.wireOp",EDGE,"E72.1");var subQ16=sQuery(id+"F12.wireOp",EDGE,"E74.1");var subQ18=sQuery(id+"F12.wireOp",EDGE,"E74.8");Q0=qUnion([makeQuery(id+"F12.imprint","IMPRINT",FACE,{"disambiguationData":[TD([[makeQuery(id+"F12.imprint","IMPRINT",EDGE,{"derivedFrom":subQ7}),1.0]])]}),makeQuery(id+"F12.imprint","IMPRINT",FACE,{"disambiguationData":[TD([[makeQuery(id+"F12.imprint","IMPRINT",EDGE,{"derivedFrom":subQ14}),1.0]])]}),makeQuery(id+"F12.imprint","IMPRINT",FACE,{"disambiguationData":[TD([[makeQuery(id+"F12.imprint","IMPRINT",EDGE,{"derivedFrom":subQ16}),1.0]])]}),makeQuery(id+"F12.imprint","IMPRINT",FACE,{"disambiguationData":[TD([[makeQuery(id+"F12.imprint","IMPRINT",EDGE,{"derivedFrom":subQ18}),-1.0]])]})]);}
            var Q1;
            Q1=makeQuery(id+"F5.boolean.opBoolean","SPLIT",FACE,{"disambiguationData":[TD([makeQuery(id+"F5.opExtrude","SWEPT_FACE",FACE,{"disambiguationData":[OSD([sQuery(id+"F4.wireOp",EDGE,"E41")])]})])],"derivedFrom":makeQuery(id+"F3.boolean.opBoolean","COPY",FACE,{"derivedFrom":makeQuery(id+"F3.opExtrude","CAP_FACE",FACE,{"disambiguationData":[OSD([sQuery(id+"F0.wireOp",EDGE,"E25.0"),sQuery(id+"F0.wireOp",EDGE,"E25.1"),sQuery(id+"F0.wireOp",EDGE,"E25.2"),sQuery(id+"F0.wireOp",EDGE,"E25.3"),sQuery(id+"F0.wireOp",EDGE,"E25.4"),sQuery(id+"F0.wireOp",EDGE,"E25.5"),sQuery(id+"F0.wireOp",EDGE,"E25.6"),sQuery(id+"F0.wireOp",EDGE,"E25.7")])],"isStart":false})})});
            extrude(context, id + "F13", {"entities" : qUnion([Q0]), "operationType" : NewBodyOperationType.REMOVE, "endBound" : BoundingType.UP_TO_SURFACE, "endBoundEntityFace" : qUnion([Q1]), "depth" : 25 * mm});
        }
        {
            var Q0;
            Q0=makeQuery(id+"F3.boolean.opBoolean","COPY",EDGE,{"derivedFrom":makeQuery(id+"F3.opExtrude","CAP_EDGE",EDGE,{"disambiguationData":[OSD([sQuery(id+"F0.wireOp",EDGE,"E25.6")])],"isStart":false})});
            var Q1;
            Q1=makeQuery(id+"F8.boolean.opBoolean","INTERSECT",EDGE,{"derivedFrom":[makeQuery(id+"F5.opExtrude","SWEPT_FACE",FACE,{"disambiguationData":[OSD([sQuery(id+"F4.wireOp",EDGE,"E30")])]}),makeQuery(id+"F8.opExtrude","CAP_FACE",FACE,{"disambiguationData":[OSD([sQuery(id+"F7.wireOp",EDGE,"E67")])],"isStart":false})]});
            var Q2;
            Q2=makeQuery(id+"F8.boolean.opBoolean","INTERSECT",EDGE,{"disambiguationData":[OD(1.0)],"derivedFrom":[makeQuery(id+"F5.opExtrude","SWEPT_FACE",FACE,{"disambiguationData":[OSD([sQuery(id+"F4.wireOp",EDGE,"E30")])]}),makeQuery(id+"F8.opExtrude","SWEPT_FACE",FACE,{"disambiguationData":[OSD([sQuery(id+"F7.wireOp",EDGE,"E67")])]})]});
            var Q3;
            {var subQ0=sQuery(id+"F4.wireOp",EDGE,"E30");Q3=makeQuery(id+"F8.boolean.opBoolean","SPLIT",EDGE,{"disambiguationData":[TD([makeQuery(id+"F5.opExtrude","SWEPT_FACE",FACE,{"disambiguationData":[OSD([sQuery(id+"F4.wireOp",EDGE,"E35.filletArc")])]})])],"derivedFrom":makeQuery(id+"F5.opExtrude","CAP_EDGE",EDGE,{"disambiguationData":[OSD([subQ0])],"isStart":false})});}
            var Q4;
            {var subQ0=sQuery(id+"F0.wireOp",EDGE,"E25.7");var subQ1=sQuery(id+"F0.wireOp",EDGE,"E25.1");var subQ2=sQuery(id+"F0.wireOp",EDGE,"E25.6");var subQ3=sQuery(id+"F0.wireOp",EDGE,"E25.5");var subQ4=sQuery(id+"F0.wireOp",EDGE,"E25.4");var subQ5=sQuery(id+"F0.wireOp",EDGE,"E25.0");var subQ6=sQuery(id+"F0.wireOp",EDGE,"E25.2");var subQ7=sQuery(id+"F0.wireOp",EDGE,"E25.3");Q4=makeQuery(id+"F8.boolean.opBoolean","INTERSECT",EDGE,{"derivedFrom":[makeQuery(id+"F5.boolean.opBoolean","SPLIT",FACE,{"disambiguationData":[TD([makeQuery(id+"F2.opExtrude","SWEPT_FACE",FACE,{"disambiguationData":[OSD([subQ5])]})])],"derivedFrom":makeQuery(id+"F3.boolean.opBoolean","COPY",FACE,{"derivedFrom":makeQuery(id+"F3.opExtrude","CAP_FACE",FACE,{"disambiguationData":[OSD([subQ5,subQ1,subQ6,subQ7,subQ4,subQ3,subQ2,subQ0])],"isStart":false})})}),makeQuery(id+"F8.opExtrude","SWEPT_FACE",FACE,{"disambiguationData":[OSD([sQuery(id+"F7.wireOp",EDGE,"E67")])]})]});}
            var Q5;
            Q5=makeQuery(id+"F8.boolean.opBoolean","INTERSECT",EDGE,{"disambiguationData":[OD(0.0)],"derivedFrom":[makeQuery(id+"F5.opExtrude","SWEPT_FACE",FACE,{"disambiguationData":[OSD([sQuery(id+"F4.wireOp",EDGE,"E30")])]}),makeQuery(id+"F8.opExtrude","SWEPT_FACE",FACE,{"disambiguationData":[OSD([sQuery(id+"F7.wireOp",EDGE,"E67")])]})]});
            fillet(context, id + "F14", {"entities" : qUnion([Q0, Q1, Q2, Q3, Q4, Q5]), "radius" : 3 * mm, "tangentPropagation" : true, "allowEdgeOverflow" : false});
        }
        {
            var Q0;
            Q0=makeQuery(id+"F1.opExtrude","CAP_EDGE",EDGE,{"disambiguationData":[OSD([sQuery(id+"F0.wireOp",EDGE,"E1.bottom")])],"isStart":false});
            fillet(context, id + "F15", {"entities" : qUnion([Q0]), "radius" : 2 * mm, "tangentPropagation" : true, "allowEdgeOverflow" : false});
        }
        {
            var Q0;
            {var subQ0=sQuery(id+"F0.wireOp",EDGE,"E22.filletArc");var subQ1=sQuery(id+"F0.wireOp",EDGE,"E7");var subQ2=sQuery(id+"F0.wireOp",EDGE,"E6");var subQ3=sQuery(id+"F0.wireOp",EDGE,"E5");var subQ4=sQuery(id+"F0.wireOp",EDGE,"E4");var subQ5=sQuery(id+"F0.wireOp",EDGE,"E1.bottom");var subQ6=sQuery(id+"F0.wireOp",EDGE,"E21.filletArc");var subQ7=sQuery(id+"F0.wireOp",EDGE,"E1.top");var subQ8=sQuery(id+"F0.wireOp",EDGE,"E1.left");var subQ9=sQuery(id+"F0.wireOp",EDGE,"E1.right");var subQ10=sQuery(id+"F0.wireOp",EDGE,"E23.filletArc");var subQ11=sQuery(id+"F0.wireOp",EDGE,"E24.filletArc");Q0=makeQuery(id+"F2.boolean.opBoolean","SPLIT",FACE,{"disambiguationData":[TD([makeQuery(id+"F1.opExtrude","SWEPT_FACE",FACE,{"disambiguationData":[OSD([subQ5])]})])],"derivedFrom":makeQuery(id+"F1.opExtrude","CAP_FACE",FACE,{"disambiguationData":[OSD([subQ5,subQ7,subQ8,subQ9,subQ4,subQ3,subQ2,subQ1,subQ6,subQ0,subQ10,subQ11])],"isStart":true})});}
            var sketch = newSketch(context, id + "F16", { "sketchPlane" : qUnion([Q0])});
            skCircle(sketch, "E79", {"center": v(0, 120) * mm, "radius": 6 * mm});
            skArc(sketch, "E80", {"start": v(15, 120) * mm, "mid": v(0, 135) * mm, "end": v(-15, 120) * mm});
            skLineSegment(sketch, "E81", {"start": v(-15, 120) * mm, "end": v(-15, 108) * mm});
            skLineSegment(sketch, "E82", {"start": v(-15, 108) * mm, "end": v(-33, 90) * mm});
            skLineSegment(sketch, "E83", {"start": v(0, 120) * mm, "end": v(0, 90) * mm, "construction": true});
            skLineSegment(sketch, "E84", {"start": v(15, 108) * mm, "end": v(33, 90) * mm});
            skLineSegment(sketch, "E85", {"start": v(-80, 0) * mm, "end": v(80, 0) * mm, "construction": true});
            skArc(sketch, "E86.MirrorCS", {"start": v(15, -120) * mm, "mid": v(0, -135) * mm, "end": v(-15, -120) * mm});
            skLineSegment(sketch, "E87.MirrorCS", {"start": v(-15, -120) * mm, "end": v(-15, -108) * mm});
            skCircle(sketch, "E88.MirrorC", {"center": v(0, -120) * mm, "radius": 6 * mm});
            skLineSegment(sketch, "E89.MirrorCS", {"start": v(15, -120) * mm, "end": v(15, -108) * mm, "construction": true});
            skLineSegment(sketch, "E90", {"start": v(15, 120) * mm, "end": v(15, 108) * mm});
            skLineSegment(sketch, "E91.MirrorCS", {"start": v(15, -120) * mm, "end": v(15, -108) * mm});
            skLineSegment(sketch, "E92.MirrorCS", {"start": v(-15, -108) * mm, "end": v(-33, -90) * mm});
            skLineSegment(sketch, "E93.MirrorCS", {"start": v(15, -108) * mm, "end": v(33, -90) * mm});
            skLineSegment(sketch, "E94.MirrorCS", {"start": v(15, 120) * mm, "end": v(15, 108) * mm, "construction": true});
            skLineSegment(sketch, "E95.MirrorCS", {"start": v(15, 92.25) * mm, "end": v(33, 74.25) * mm});
            skSolve(sketch);
        }
        {
            var Q0;
            Q0=makeQuery(id+"F16.imprint","IMPRINT",FACE,{"disambiguationData":[TD([[makeQuery(id+"F16.imprint","IMPRINT",EDGE,{"derivedFrom":sQuery(id+"F16.wireOp",EDGE,"E91.MirrorCS")}),1.0]])]});
            var Q1;
            Q1=makeQuery(id+"F16.imprint","IMPRINT",FACE,{"disambiguationData":[TD([[makeQuery(id+"F16.imprint","IMPRINT",EDGE,{"derivedFrom":makeQuery(id+"F1.opExtrude","CAP_EDGE",EDGE,{"disambiguationData":[OSD([sQuery(id+"F0.wireOp",EDGE,"E1.left")])],"isStart":true})}),-1.0]])]});
            var Q2;
            Q2=makeQuery(id+"F16.imprint","IMPRINT",FACE,{"disambiguationData":[TD([[makeQuery(id+"F16.imprint","IMPRINT",EDGE,{"derivedFrom":sQuery(id+"F16.wireOp",EDGE,"E79")}),-1.0]])]});
            var Q3;
            Q3=makeQuery(id+"F2.opExtrude","CAP_FACE",FACE,{"disambiguationData":[OSD([sQuery(id+"F0.wireOp",EDGE,"E12"),sQuery(id+"F0.wireOp",EDGE,"E13"),sQuery(id+"F0.wireOp",EDGE,"E14"),sQuery(id+"F0.wireOp",EDGE,"E15"),sQuery(id+"F0.wireOp",EDGE,"E17.filletArc"),sQuery(id+"F0.wireOp",EDGE,"E18.filletArc"),sQuery(id+"F0.wireOp",EDGE,"E19.filletArc"),sQuery(id+"F0.wireOp",EDGE,"E20.filletArc"),sQuery(id+"F0.wireOp",EDGE,"E25.0"),sQuery(id+"F0.wireOp",EDGE,"E25.1"),sQuery(id+"F0.wireOp",EDGE,"E25.2"),sQuery(id+"F0.wireOp",EDGE,"E25.3"),sQuery(id+"F0.wireOp",EDGE,"E25.4"),sQuery(id+"F0.wireOp",EDGE,"E25.5"),sQuery(id+"F0.wireOp",EDGE,"E25.6"),sQuery(id+"F0.wireOp",EDGE,"E25.7")])],"isStart":false});
            extrude(context, id + "F17", {"entities" : qUnion([Q0, Q1, Q2]), "endBound" : BoundingType.UP_TO_SURFACE, "endBoundEntityFace" : qUnion([Q3]), "depth" : 25 * mm});
        }
    });
